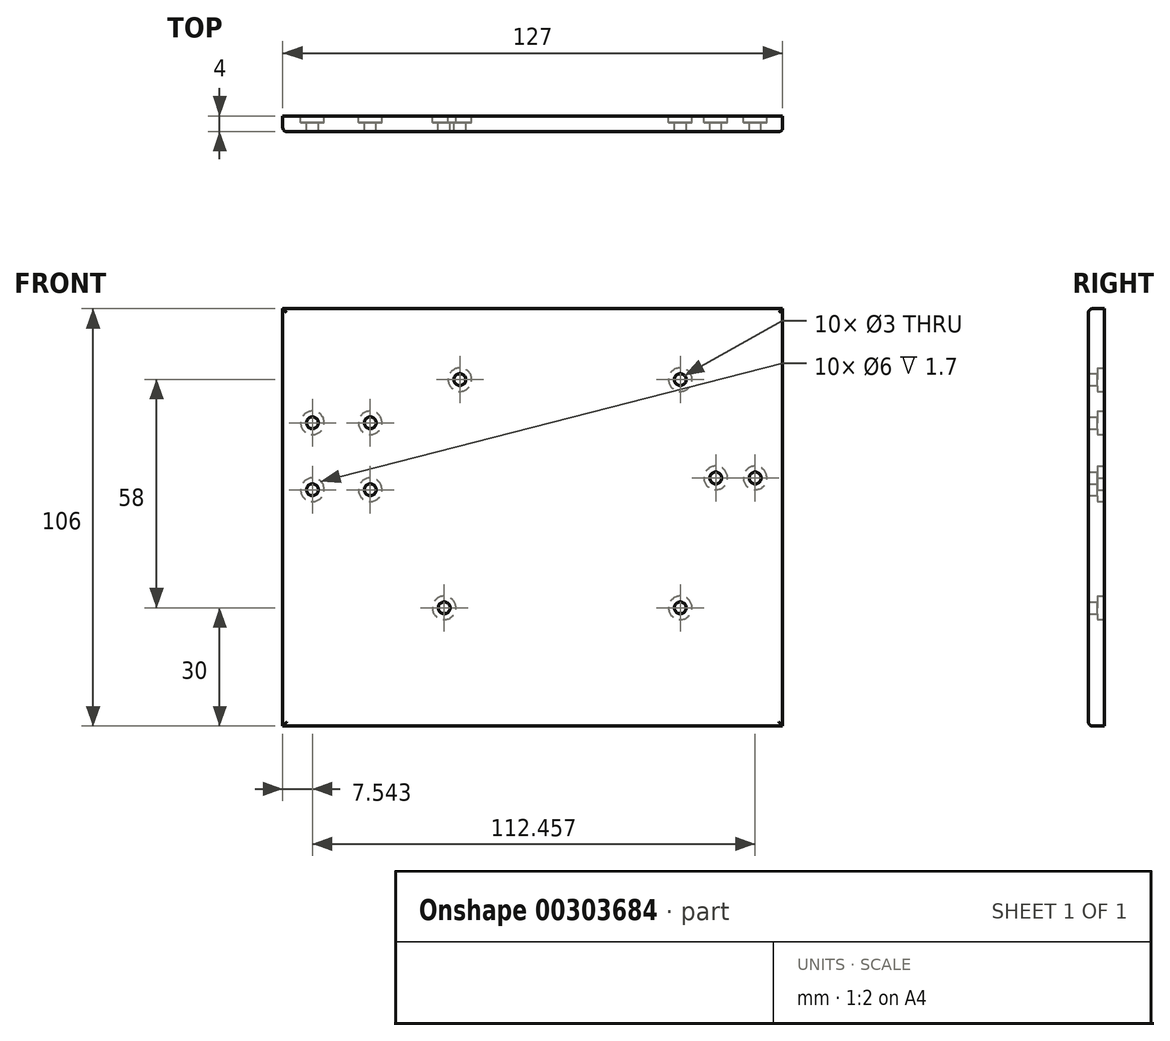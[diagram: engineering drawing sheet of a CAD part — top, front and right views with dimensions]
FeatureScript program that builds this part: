
annotation { "Feature Type Name" : "Feature", "Feature Type Description" : "" }
export const myFeature = defineFeature(function(context is Context, id is Id, definition is map)
    precondition{}
    {
        {
            var Q0;
            Q0=qCreatedBy(makeId("Front.planeOp"),FACE);
            var sketch = newSketch(context, id + "F0", { "sketchPlane" : qUnion([Q0])});
            skLineSegment(sketch, "E0.bottom", {"start": v(-62.5, 53) * mm, "end": v(64.5, 53) * mm});
            skLineSegment(sketch, "E0.top", {"start": v(-62.5, -53) * mm, "end": v(64.5, -53) * mm});
            skLineSegment(sketch, "E0.left", {"start": v(-62.5, 53) * mm, "end": v(-62.5, -53) * mm});
            skLineSegment(sketch, "E0.right", {"start": v(64.5, 53) * mm, "end": v(64.5, -53) * mm});
            skPoint(sketch, "E1", {"position": v(-54.96, 24) * mm});
            skPoint(sketch, "E2", {"position": v(-40.29, 24) * mm});
            skPoint(sketch, "E3", {"position": v(-40.29, 7) * mm});
            skPoint(sketch, "E4", {"position": v(-54.96, 7) * mm});
            skPoint(sketch, "E5", {"position": v(47.5, 10) * mm});
            skPoint(sketch, "E6", {"position": v(57.5, 10) * mm});
            skPoint(sketch, "E7", {"position": v(-17.5, 35) * mm});
            skPoint(sketch, "E8", {"position": v(38.5, 35) * mm});
            skPoint(sketch, "E9", {"position": v(-21.5, -23) * mm});
            skPoint(sketch, "E10", {"position": v(38.5, -23) * mm});
            skCircle(sketch, "E11", {"center": v(-17.5, 35) * mm, "radius": 1.5 * mm});
            skCircle(sketch, "E12", {"center": v(38.5, 35) * mm, "radius": 1.5 * mm});
            skCircle(sketch, "E13", {"center": v(47.5, 10) * mm, "radius": 1.5 * mm});
            skCircle(sketch, "E14", {"center": v(57.5, 10) * mm, "radius": 1.5 * mm});
            skCircle(sketch, "E15", {"center": v(-40.29, 24) * mm, "radius": 1.5 * mm});
            skCircle(sketch, "E16", {"center": v(-40.29, 7) * mm, "radius": 1.5 * mm});
            skCircle(sketch, "E17", {"center": v(-54.96, 24) * mm, "radius": 1.5 * mm});
            skCircle(sketch, "E18", {"center": v(38.5, -23) * mm, "radius": 1.5 * mm});
            skCircle(sketch, "E19", {"center": v(-54.96, 7) * mm, "radius": 1.5 * mm});
            skCircle(sketch, "E20", {"center": v(-21.5, -23) * mm, "radius": 1.5 * mm});
            skSolve(sketch);
        }
        {
            var Q0;
            Q0=makeQuery(id+"F0.imprint","IMPRINT",FACE,{"disambiguationData":[TD([[makeQuery(id+"F0.imprint","IMPRINT",EDGE,{"derivedFrom":sQuery(id+"F0.wireOp",EDGE,"E0.bottom")}),-1.0]])]});
            extrude(context, id + "F1", {"entities" : qUnion([Q0]), "depth" : 4 * mm});
        }
        {
            var Q0;
            Q0=makeQuery(id+"F1.opExtrude","CAP_EDGE",EDGE,{"disambiguationData":[OSD([sQuery(id+"F0.wireOp",EDGE,"E0.bottom")])],"isStart":false});
            var Q1;
            Q1=makeQuery(id+"F1.opExtrude","CAP_EDGE",EDGE,{"disambiguationData":[OSD([sQuery(id+"F0.wireOp",EDGE,"E0.left")])],"isStart":false});
            var Q2;
            Q2=makeQuery(id+"F1.opExtrude","CAP_EDGE",EDGE,{"disambiguationData":[OSD([sQuery(id+"F0.wireOp",EDGE,"E0.right")])],"isStart":false});
            var Q3;
            Q3=makeQuery(id+"F1.opExtrude","CAP_EDGE",EDGE,{"disambiguationData":[OSD([sQuery(id+"F0.wireOp",EDGE,"E0.top")])],"isStart":false});
            fillet(context, id + "F2", {"entities" : qUnion([Q0, Q1, Q2, Q3]), "radius" : 1 * mm, "tangentPropagation" : true, "allowEdgeOverflow" : false});
        }
        {
            var Q0;
            Q0=makeQuery(id+"F1.opExtrude","CAP_FACE",FACE,{"disambiguationData":[OSD([sQuery(id+"F0.wireOp",EDGE,"E0.bottom"),sQuery(id+"F0.wireOp",EDGE,"E0.top"),sQuery(id+"F0.wireOp",EDGE,"E0.left"),sQuery(id+"F0.wireOp",EDGE,"E0.right"),sQuery(id+"F0.wireOp",EDGE,"E11"),sQuery(id+"F0.wireOp",EDGE,"E12"),sQuery(id+"F0.wireOp",EDGE,"E13"),sQuery(id+"F0.wireOp",EDGE,"E14"),sQuery(id+"F0.wireOp",EDGE,"E15"),sQuery(id+"F0.wireOp",EDGE,"E16"),sQuery(id+"F0.wireOp",EDGE,"E17"),sQuery(id+"F0.wireOp",EDGE,"E18"),sQuery(id+"F0.wireOp",EDGE,"E19"),sQuery(id+"F0.wireOp",EDGE,"E20")])],"isStart":true});
            var sketch = newSketch(context, id + "F3", { "sketchPlane" : qUnion([Q0])});
            skCircle(sketch, "E21", {"center": v(-38.5, -23) * mm, "radius": 3 * mm});
            skCircle(sketch, "E22", {"center": v(-57.5, 10) * mm, "radius": 3 * mm});
            skCircle(sketch, "E23", {"center": v(-47.5, 10) * mm, "radius": 3 * mm});
            skCircle(sketch, "E24", {"center": v(-38.5, 35) * mm, "radius": 3 * mm});
            skCircle(sketch, "E25", {"center": v(17.5, 35) * mm, "radius": 3 * mm});
            skCircle(sketch, "E26", {"center": v(40.29, 24) * mm, "radius": 3 * mm});
            skCircle(sketch, "E27", {"center": v(54.96, 24) * mm, "radius": 3 * mm});
            skCircle(sketch, "E28", {"center": v(40.29, 7) * mm, "radius": 3 * mm});
            skCircle(sketch, "E29", {"center": v(54.96, 7) * mm, "radius": 3 * mm});
            skCircle(sketch, "E30", {"center": v(21.5, -23) * mm, "radius": 3 * mm});
            skSolve(sketch);
        }
        {
            var Q0;
            Q0=makeQuery(id+"F3.imprint","IMPRINT",FACE,{"disambiguationData":[TD([[makeQuery(id+"F3.imprint","IMPRINT",EDGE,{"derivedFrom":sQuery(id+"F3.wireOp",EDGE,"E21")}),1.0]])]});
            var Q1;
            Q1=makeQuery(id+"F3.imprint","IMPRINT",FACE,{"disambiguationData":[TD([[makeQuery(id+"F3.imprint","IMPRINT",EDGE,{"derivedFrom":sQuery(id+"F3.wireOp",EDGE,"E22")}),1.0]])]});
            var Q2;
            Q2=makeQuery(id+"F3.imprint","IMPRINT",FACE,{"disambiguationData":[TD([[makeQuery(id+"F3.imprint","IMPRINT",EDGE,{"derivedFrom":sQuery(id+"F3.wireOp",EDGE,"E23")}),1.0]])]});
            var Q3;
            Q3=makeQuery(id+"F3.imprint","IMPRINT",FACE,{"disambiguationData":[TD([[makeQuery(id+"F3.imprint","IMPRINT",EDGE,{"derivedFrom":sQuery(id+"F3.wireOp",EDGE,"E24")}),1.0]])]});
            var Q4;
            Q4=makeQuery(id+"F3.imprint","IMPRINT",FACE,{"disambiguationData":[TD([[makeQuery(id+"F3.imprint","IMPRINT",EDGE,{"derivedFrom":sQuery(id+"F3.wireOp",EDGE,"E25")}),1.0]])]});
            var Q5;
            Q5=makeQuery(id+"F3.imprint","IMPRINT",FACE,{"disambiguationData":[TD([[makeQuery(id+"F3.imprint","IMPRINT",EDGE,{"derivedFrom":sQuery(id+"F3.wireOp",EDGE,"E26")}),1.0]])]});
            var Q6;
            Q6=makeQuery(id+"F3.imprint","IMPRINT",FACE,{"disambiguationData":[TD([[makeQuery(id+"F3.imprint","IMPRINT",EDGE,{"derivedFrom":sQuery(id+"F3.wireOp",EDGE,"E27")}),1.0]])]});
            var Q7;
            Q7=makeQuery(id+"F3.imprint","IMPRINT",FACE,{"disambiguationData":[TD([[makeQuery(id+"F3.imprint","IMPRINT",EDGE,{"derivedFrom":sQuery(id+"F3.wireOp",EDGE,"E29")}),1.0]])]});
            var Q8;
            Q8=makeQuery(id+"F3.imprint","IMPRINT",FACE,{"disambiguationData":[TD([[makeQuery(id+"F3.imprint","IMPRINT",EDGE,{"derivedFrom":sQuery(id+"F3.wireOp",EDGE,"E28")}),1.0]])]});
            var Q9;
            Q9=makeQuery(id+"F3.imprint","IMPRINT",FACE,{"disambiguationData":[TD([[makeQuery(id+"F3.imprint","IMPRINT",EDGE,{"derivedFrom":sQuery(id+"F3.wireOp",EDGE,"E30")}),1.0]])]});
            extrude(context, id + "F4", {"entities" : qUnion([Q0, Q1, Q2, Q3, Q4, Q5, Q6, Q7, Q8, Q9]), "operationType" : NewBodyOperationType.REMOVE, "oppositeDirection" : true, "depth" : 1.7 * mm});
        }
    });
